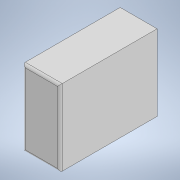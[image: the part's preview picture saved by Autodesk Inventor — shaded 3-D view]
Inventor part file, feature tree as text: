
AUTODESK INVENTOR PART (.ipt)
format: ipt  version: 2020.1 (Build 241239000, 239)  size: 117,248 bytes
history: native  units: mm
features: other x1, extrude x1, fillet x1, sketch x1
ambient origin geometry x8: Origin, YZ Plane, XZ Plane, XY Plane, X Axis, Y Axis, Z Axis, Center Point
bodies: Solid1 (feature_tree)
feature tree (4):
  parser-record x1  (decoder bookkeeping rows leaked as tree rows — omitted from the tree; the rows remain in map.json)
  extrude  "Extrusion1"  Depth=7.8mm
  fillet  "Fillet1"  Radius=10.0mm
  sketch  "Sketch1"  dims[d0=3.8mm d1=7.8mm d2=10.0mm d3=0.0mm d4=0.25mm]
note: 1 file-system path scrubbed to <path> (originals preserved in map.json)
